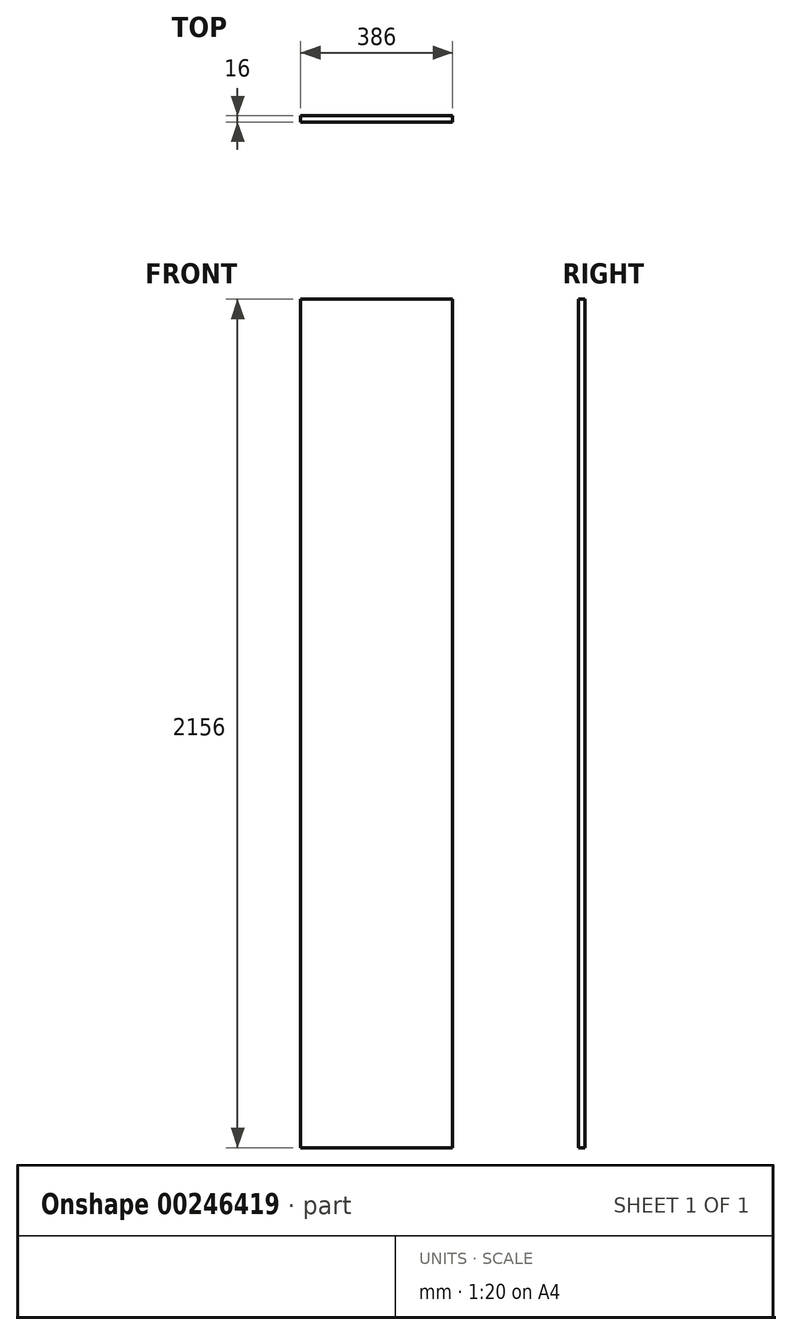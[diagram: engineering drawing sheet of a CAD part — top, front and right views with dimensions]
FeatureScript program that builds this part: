
annotation { "Feature Type Name" : "Feature", "Feature Type Description" : "" }
export const myFeature = defineFeature(function(context is Context, id is Id, definition is map)
    precondition{}
    {
        {
            var Q0;
            Q0=qCreatedBy(makeId("Front.planeOp"),FACE);
            var sketch = newSketch(context, id + "F0", { "sketchPlane" : qUnion([Q0])});
            skLineSegment(sketch, "E0.bottom", {"start": v(0, 0) * mm, "end": v(386, 0) * mm});
            skLineSegment(sketch, "E0.top", {"start": v(0, 2156) * mm, "end": v(386, 2156) * mm});
            skLineSegment(sketch, "E0.left", {"start": v(0, 0) * mm, "end": v(0, 2156) * mm});
            skLineSegment(sketch, "E0.right", {"start": v(386, 0) * mm, "end": v(386, 2156) * mm});
            skSolve(sketch);
        }
        {
            var Q0;
            Q0 = qSketchRegion(id + "F0", true);
            extrude(context, id + "F1", {"entities" : qUnion([Q0]), "depth" : 16 * mm});
        }
    });
